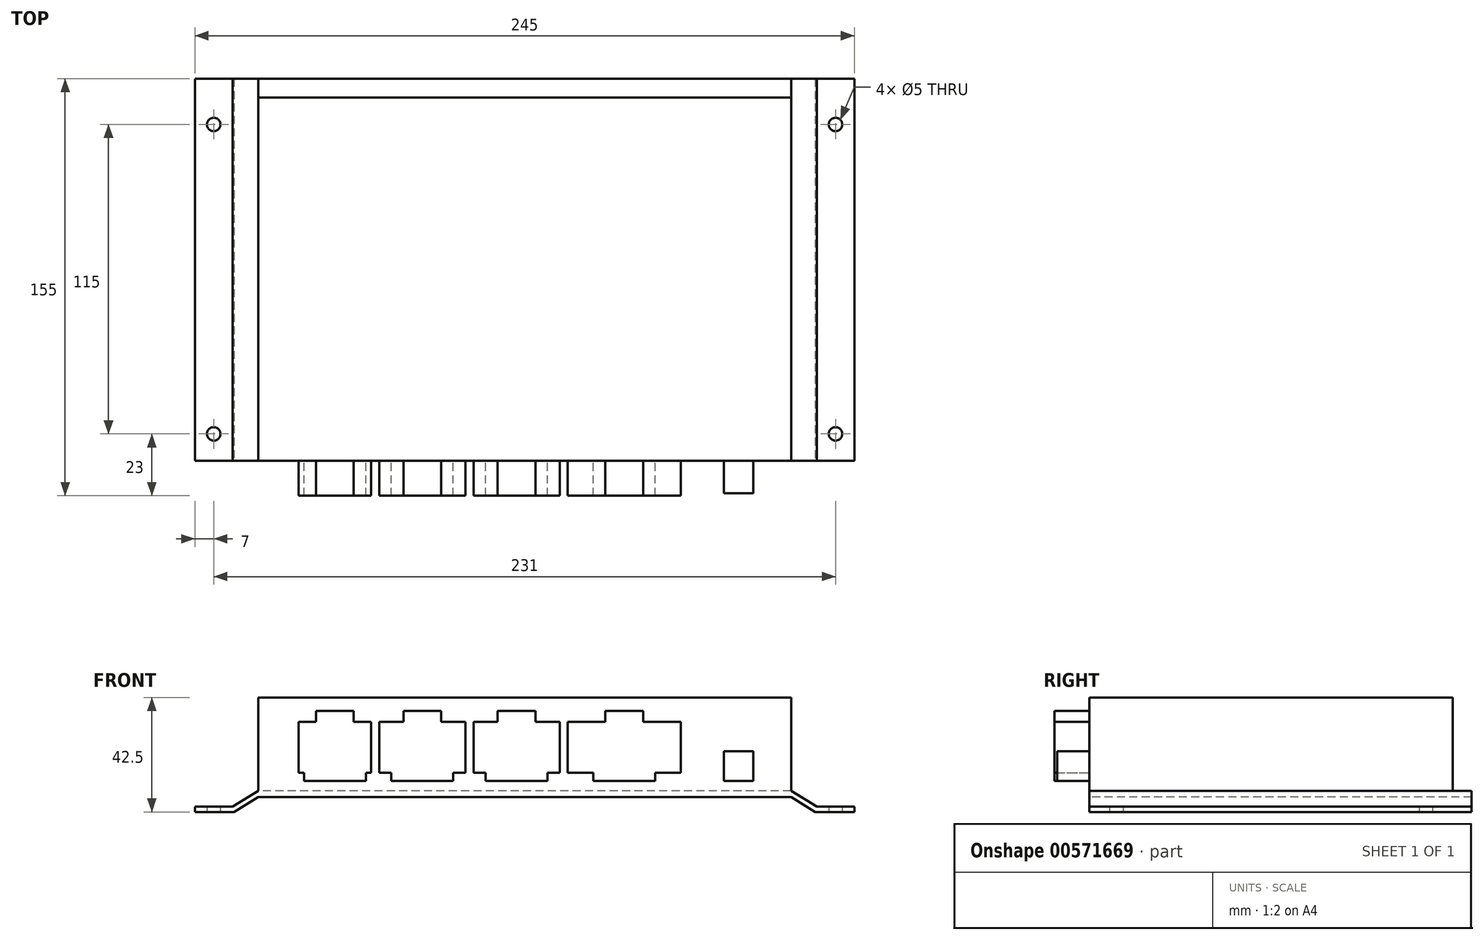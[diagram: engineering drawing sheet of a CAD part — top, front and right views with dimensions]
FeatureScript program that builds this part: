
annotation { "Feature Type Name" : "Feature", "Feature Type Description" : "" }
export const myFeature = defineFeature(function(context is Context, id is Id, definition is map)
    precondition{}
    {
        {
            var Q0;
            Q0=qCreatedBy(makeId("Top.planeOp"),FACE);
            var sketch = newSketch(context, id + "F0", { "sketchPlane" : qUnion([Q0])});
            skLineSegment(sketch, "E0.bottom", {"start": v(99, 67.5) * mm, "end": v(-99, 67.5) * mm});
            skLineSegment(sketch, "E0.top", {"start": v(99, -67.5) * mm, "end": v(-99, -67.5) * mm});
            skLineSegment(sketch, "E0.left", {"start": v(99, 67.5) * mm, "end": v(99, -67.5) * mm});
            skLineSegment(sketch, "E0.right", {"start": v(-99, 67.5) * mm, "end": v(-99, -67.5) * mm});
            skPoint(sketch, "E0.middle", {"position": v(0, 0) * mm});
            skSolve(sketch);
        }
        {
            var Q0;
            Q0=makeQuery(id+"F0.imprint","IMPRINT",FACE,{"disambiguationData":[TD([[makeQuery(id+"F0.imprint","IMPRINT",EDGE,{"derivedFrom":sQuery(id+"F0.wireOp",EDGE,"E0.bottom")}),1.0]])]});
            extrude(context, id + "F1", {"entities" : qUnion([Q0]), "depth" : 37 * mm, "offsetDistance" : 25 * mm});
        }
        {
            var Q0;
            Q0=makeQuery(id+"F1.opExtrude","SWEPT_FACE",FACE,{"disambiguationData":[OSD([sQuery(id+"F0.wireOp",EDGE,"E0.top")])]});
            var sketch = newSketch(context, id + "F2", { "sketchPlane" : qUnion([Q0])});
            skLineSegment(sketch, "E1", {"start": v(-122.5, -3.5) * mm, "end": v(-122.5, -5.5) * mm});
            skLineSegment(sketch, "E2", {"start": v(-122.5, -5.5) * mm, "end": v(-107.93, -5.5) * mm});
            skLineSegment(sketch, "E3", {"start": v(-107.93, -5.5) * mm, "end": v(-99, 0) * mm});
            skLineSegment(sketch, "E4", {"start": v(-122.5, -3.5) * mm, "end": v(-108.5, -3.5) * mm});
            skLineSegment(sketch, "E5", {"start": v(-108.5, -3.5) * mm, "end": v(-99, 2.35) * mm});
            skLineSegment(sketch, "E6", {"start": v(-99, 2.35) * mm, "end": v(-99, 0) * mm});
            skLineSegment(sketch, "E7", {"start": v(0, 37) * mm, "end": v(0, 0) * mm, "construction": true});
            skLineSegment(sketch, "E8.MirrorCS", {"start": v(99, 2.35) * mm, "end": v(99, 0) * mm});
            skLineSegment(sketch, "E9.MirrorCS", {"start": v(107.93, -5.5) * mm, "end": v(99, 0) * mm});
            skLineSegment(sketch, "E10.MirrorCS", {"start": v(108.5, -3.5) * mm, "end": v(99, 2.35) * mm});
            skLineSegment(sketch, "E11.MirrorCS", {"start": v(122.5, -3.5) * mm, "end": v(108.5, -3.5) * mm});
            skLineSegment(sketch, "E12.MirrorCS", {"start": v(122.5, -5.5) * mm, "end": v(107.93, -5.5) * mm});
            skLineSegment(sketch, "E13.MirrorCS", {"start": v(122.5, -3.5) * mm, "end": v(122.5, -5.5) * mm});
            skSolve(sketch);
        }
        {
            var Q0;
            Q0=makeQuery(id+"F2.imprint","IMPRINT",FACE,{"disambiguationData":[TD([[makeQuery(id+"F2.imprint","IMPRINT",EDGE,{"derivedFrom":sQuery(id+"F2.wireOp",EDGE,"E1")}),1.0]])]});
            var Q1;
            Q1=makeQuery(id+"F2.imprint","IMPRINT",FACE,{"disambiguationData":[TD([[makeQuery(id+"F2.imprint","IMPRINT",EDGE,{"derivedFrom":sQuery(id+"F2.wireOp",EDGE,"E8.MirrorCS")}),1.0]])]});
            var Q2;
            Q2=makeQuery(id+"F1.opExtrude","SWEPT_FACE",FACE,{"disambiguationData":[OSD([sQuery(id+"F0.wireOp",EDGE,"E0.bottom")])]});
            extrude(context, id + "F3", {"entities" : qUnion([Q0, Q1]), "operationType" : NewBodyOperationType.ADD, "endBound" : BoundingType.UP_TO_SURFACE, "oppositeDirection" : true, "depth" : 25 * mm, "endBoundEntityFace" : qUnion([Q2]), "offsetDistance" : 25 * mm});
        }
        {
            var Q0;
            Q0=makeQuery(id+"F3.opExtrude","SWEPT_FACE",FACE,{"disambiguationData":[OSD([sQuery(id+"F2.wireOp",EDGE,"E2")])]});
            var sketch = newSketch(context, id + "F4", { "sketchPlane" : qUnion([Q0])});
            skLineSegment(sketch, "E14.bottom", {"start": v(115.5, 57.5) * mm, "end": v(-115.5, 57.5) * mm, "construction": true});
            skLineSegment(sketch, "E14.top", {"start": v(115.5, -57.5) * mm, "end": v(-115.5, -57.5) * mm, "construction": true});
            skLineSegment(sketch, "E14.left", {"start": v(115.5, 57.5) * mm, "end": v(115.5, -57.5) * mm, "construction": true});
            skLineSegment(sketch, "E14.right", {"start": v(-115.5, 57.5) * mm, "end": v(-115.5, -57.5) * mm, "construction": true});
            skPoint(sketch, "E14.middle", {"position": v(0, 0) * mm});
            skCircle(sketch, "E15", {"center": v(-115.5, 57.5) * mm, "radius": 2.5 * mm});
            skCircle(sketch, "E16", {"center": v(-115.5, -57.5) * mm, "radius": 2.5 * mm});
            skCircle(sketch, "E17", {"center": v(115.5, -57.5) * mm, "radius": 2.5 * mm});
            skCircle(sketch, "E18", {"center": v(115.5, 57.5) * mm, "radius": 2.5 * mm});
            skSolve(sketch);
        }
        {
            var Q0;
            Q0=makeQuery(id+"F4.imprint","IMPRINT",FACE,{"disambiguationData":[TD([[makeQuery(id+"F4.imprint","IMPRINT",EDGE,{"derivedFrom":sQuery(id+"F4.wireOp",EDGE,"E15")}),1.0]])]});
            var Q1;
            Q1=makeQuery(id+"F4.imprint","IMPRINT",FACE,{"disambiguationData":[TD([[makeQuery(id+"F4.imprint","IMPRINT",EDGE,{"derivedFrom":sQuery(id+"F4.wireOp",EDGE,"E16")}),1.0]])]});
            var Q2;
            Q2=makeQuery(id+"F4.imprint","IMPRINT",FACE,{"disambiguationData":[TD([[makeQuery(id+"F4.imprint","IMPRINT",EDGE,{"derivedFrom":sQuery(id+"F4.wireOp",EDGE,"E17")}),1.0]])]});
            var Q3;
            Q3=makeQuery(id+"F4.imprint","IMPRINT",FACE,{"disambiguationData":[TD([[makeQuery(id+"F4.imprint","IMPRINT",EDGE,{"derivedFrom":sQuery(id+"F4.wireOp",EDGE,"E18")}),1.0]])]});
            extrude(context, id + "F5", {"entities" : qUnion([Q0, Q1, Q2, Q3]), "operationType" : NewBodyOperationType.REMOVE, "oppositeDirection" : true, "depth" : 25 * mm, "offsetDistance" : 25 * mm});
        }
        {
            var Q0;
            {var subQ0=sQuery(id+"F0.wireOp",EDGE,"E0.bottom");Q0=makeQuery(id+"F3.boolean.opBoolean","MERGE",FACE,{"derivedFrom":[makeQuery(id+"F1.opExtrude","SWEPT_FACE",FACE,{"disambiguationData":[OSD([subQ0])]}),makeQuery(id+"F3.opExtrude","CAP_FACE",FACE,{"disambiguationData":[OSD([subQ0]),OD(0.0)],"isStart":false}),makeQuery(id+"F3.opExtrude","CAP_FACE",FACE,{"disambiguationData":[OSD([subQ0]),OD(1.0)],"isStart":false})]});}
            var sketch = newSketch(context, id + "F6", { "sketchPlane" : qUnion([Q0])});
            skLineSegment(sketch, "E19", {"start": v(-107.93, -5.5) * mm, "end": v(-122.5, -5.5) * mm});
            skLineSegment(sketch, "E20", {"start": v(-122.5, -5.5) * mm, "end": v(-122.5, -3.5) * mm});
            skLineSegment(sketch, "E21", {"start": v(-122.5, -3.5) * mm, "end": v(-108.5, -3.5) * mm});
            skLineSegment(sketch, "E22", {"start": v(-108.5, -3.5) * mm, "end": v(-99, 2.35) * mm});
            skLineSegment(sketch, "E23", {"start": v(-99, 2.35) * mm, "end": v(99, 2.35) * mm});
            skLineSegment(sketch, "E24", {"start": v(99, 2.35) * mm, "end": v(108.5, -3.5) * mm});
            skLineSegment(sketch, "E25", {"start": v(108.5, -3.5) * mm, "end": v(122.5, -3.5) * mm});
            skLineSegment(sketch, "E26", {"start": v(122.5, -3.5) * mm, "end": v(122.5, -5.5) * mm});
            skLineSegment(sketch, "E27", {"start": v(122.5, -5.5) * mm, "end": v(107.93, -5.5) * mm});
            skLineSegment(sketch, "E28", {"start": v(107.93, -5.5) * mm, "end": v(99, 0) * mm});
            skLineSegment(sketch, "E29", {"start": v(99, 0) * mm, "end": v(-99, 0) * mm});
            skLineSegment(sketch, "E30", {"start": v(-99, 0) * mm, "end": v(-107.93, -5.5) * mm});
            skSolve(sketch);
        }
        {
            var Q0;
            Q0 = qSketchRegion(id + "F6", true);
            extrude(context, id + "F7", {"entities" : qUnion([Q0]), "operationType" : NewBodyOperationType.ADD, "depth" : 7 * mm, "offsetDistance" : 25 * mm});
        }
        {
            var Q0;
            Q0=makeQuery(id+"F3.boolean.opBoolean","MERGE",FACE,{"derivedFrom":[makeQuery(id+"F1.opExtrude","SWEPT_FACE",FACE,{"disambiguationData":[OSD([sQuery(id+"F0.wireOp",EDGE,"E0.top")])]}),makeQuery(id+"F3.opExtrude","CAP_FACE",FACE,{"disambiguationData":[OSD([sQuery(id+"F2.wireOp",EDGE,"E1"),sQuery(id+"F2.wireOp",EDGE,"E2"),sQuery(id+"F2.wireOp",EDGE,"E3"),sQuery(id+"F2.wireOp",EDGE,"E4"),sQuery(id+"F2.wireOp",EDGE,"E5"),sQuery(id+"F2.wireOp",EDGE,"E6")])],"isStart":true}),makeQuery(id+"F3.opExtrude","CAP_FACE",FACE,{"disambiguationData":[OSD([sQuery(id+"F2.wireOp",EDGE,"E8.MirrorCS"),sQuery(id+"F2.wireOp",EDGE,"E9.MirrorCS"),sQuery(id+"F2.wireOp",EDGE,"E10.MirrorCS"),sQuery(id+"F2.wireOp",EDGE,"E11.MirrorCS"),sQuery(id+"F2.wireOp",EDGE,"E12.MirrorCS"),sQuery(id+"F2.wireOp",EDGE,"E13.MirrorCS")])],"isStart":true})]});
            var sketch = newSketch(context, id + "F8", { "sketchPlane" : qUnion([Q0])});
            skLineSegment(sketch, "E31", {"start": v(-84, 28) * mm, "end": v(-84, 9) * mm});
            skLineSegment(sketch, "E32", {"start": v(-84, 9) * mm, "end": v(-82, 9) * mm});
            skLineSegment(sketch, "E33", {"start": v(-82, 9) * mm, "end": v(-82, 6) * mm});
            skLineSegment(sketch, "E34", {"start": v(-82, 6) * mm, "end": v(-59, 6) * mm});
            skLineSegment(sketch, "E35", {"start": v(-59, 6) * mm, "end": v(-59, 9) * mm});
            skLineSegment(sketch, "E36", {"start": v(-59, 9) * mm, "end": v(-57, 9) * mm});
            skLineSegment(sketch, "E37", {"start": v(-57, 9) * mm, "end": v(-57, 28) * mm});
            skLineSegment(sketch, "E38", {"start": v(-57, 28) * mm, "end": v(-63.5, 28) * mm});
            skLineSegment(sketch, "E39", {"start": v(-63.5, 28) * mm, "end": v(-63.5, 32) * mm});
            skLineSegment(sketch, "E40", {"start": v(-63.5, 32) * mm, "end": v(-77.5, 32) * mm});
            skLineSegment(sketch, "E41", {"start": v(-77.5, 32) * mm, "end": v(-77.5, 28) * mm});
            skLineSegment(sketch, "E42", {"start": v(-77.5, 28) * mm, "end": v(-84, 28) * mm});
            skLineSegment(sketch, "E43", {"start": v(-54, 28) * mm, "end": v(-54, 9) * mm});
            skLineSegment(sketch, "E44", {"start": v(-54, 9) * mm, "end": v(-49.5, 9) * mm});
            skLineSegment(sketch, "E45", {"start": v(-49.5, 9) * mm, "end": v(-49.5, 6) * mm});
            skLineSegment(sketch, "E46", {"start": v(-49.5, 6) * mm, "end": v(-26.5, 6) * mm});
            skLineSegment(sketch, "E47", {"start": v(-26.5, 6) * mm, "end": v(-26.5, 9) * mm});
            skLineSegment(sketch, "E48", {"start": v(-26.5, 9) * mm, "end": v(-22, 9) * mm});
            skLineSegment(sketch, "E49", {"start": v(-22, 9) * mm, "end": v(-22, 28) * mm});
            skLineSegment(sketch, "E50", {"start": v(-22, 28) * mm, "end": v(-31, 28) * mm});
            skLineSegment(sketch, "E51", {"start": v(-31, 28) * mm, "end": v(-31, 32) * mm});
            skLineSegment(sketch, "E52", {"start": v(-31, 32) * mm, "end": v(-45, 32) * mm});
            skLineSegment(sketch, "E53", {"start": v(-45, 32) * mm, "end": v(-45, 28) * mm});
            skLineSegment(sketch, "E54", {"start": v(-45, 28) * mm, "end": v(-54, 28) * mm});
            skLineSegment(sketch, "E55", {"start": v(-19, 28) * mm, "end": v(-19, 9) * mm});
            skLineSegment(sketch, "E56", {"start": v(-19, 9) * mm, "end": v(-14.5, 9) * mm});
            skLineSegment(sketch, "E57", {"start": v(-14.5, 9) * mm, "end": v(-14.5, 6) * mm});
            skLineSegment(sketch, "E58", {"start": v(-14.5, 6) * mm, "end": v(8.5, 6) * mm});
            skLineSegment(sketch, "E59", {"start": v(8.5, 6) * mm, "end": v(8.5, 9) * mm});
            skLineSegment(sketch, "E60", {"start": v(8.5, 9) * mm, "end": v(13, 9) * mm});
            skLineSegment(sketch, "E61", {"start": v(13, 9) * mm, "end": v(13, 28) * mm});
            skLineSegment(sketch, "E62", {"start": v(13, 28) * mm, "end": v(4, 28) * mm});
            skLineSegment(sketch, "E63", {"start": v(4, 28) * mm, "end": v(4, 32) * mm});
            skLineSegment(sketch, "E64", {"start": v(4, 32) * mm, "end": v(-10, 32) * mm});
            skLineSegment(sketch, "E65", {"start": v(-10, 32) * mm, "end": v(-10, 28) * mm});
            skLineSegment(sketch, "E66", {"start": v(-10, 28) * mm, "end": v(-19, 28) * mm});
            skLineSegment(sketch, "E67", {"start": v(16, 28) * mm, "end": v(16, 9) * mm});
            skLineSegment(sketch, "E68", {"start": v(16, 9) * mm, "end": v(25.5, 9) * mm});
            skLineSegment(sketch, "E69", {"start": v(25.5, 9) * mm, "end": v(25.5, 6) * mm});
            skLineSegment(sketch, "E70", {"start": v(25.5, 6) * mm, "end": v(48.5, 6) * mm});
            skLineSegment(sketch, "E71", {"start": v(48.5, 6) * mm, "end": v(48.5, 9) * mm});
            skLineSegment(sketch, "E72", {"start": v(48.5, 9) * mm, "end": v(58, 9) * mm});
            skLineSegment(sketch, "E73", {"start": v(58, 9) * mm, "end": v(58, 28) * mm});
            skLineSegment(sketch, "E74", {"start": v(58, 28) * mm, "end": v(44, 28) * mm});
            skLineSegment(sketch, "E75", {"start": v(44, 28) * mm, "end": v(44, 32) * mm});
            skLineSegment(sketch, "E76", {"start": v(44, 32) * mm, "end": v(30, 32) * mm});
            skLineSegment(sketch, "E77", {"start": v(30, 32) * mm, "end": v(30, 28) * mm});
            skLineSegment(sketch, "E78", {"start": v(30, 28) * mm, "end": v(16, 28) * mm});
            skSolve(sketch);
        }
        {
            var Q0;
            Q0=makeQuery(id+"F8.imprint","IMPRINT",FACE,{"disambiguationData":[TD([[makeQuery(id+"F8.imprint","IMPRINT",EDGE,{"derivedFrom":sQuery(id+"F8.wireOp",EDGE,"E31")}),1.0]])]});
            var Q1;
            Q1=makeQuery(id+"F8.imprint","IMPRINT",FACE,{"disambiguationData":[TD([[makeQuery(id+"F8.imprint","IMPRINT",EDGE,{"derivedFrom":sQuery(id+"F8.wireOp",EDGE,"E43")}),1.0]])]});
            var Q2;
            Q2=makeQuery(id+"F8.imprint","IMPRINT",FACE,{"disambiguationData":[TD([[makeQuery(id+"F8.imprint","IMPRINT",EDGE,{"derivedFrom":sQuery(id+"F8.wireOp",EDGE,"E55")}),1.0]])]});
            var Q3;
            Q3=makeQuery(id+"F8.imprint","IMPRINT",FACE,{"disambiguationData":[TD([[makeQuery(id+"F8.imprint","IMPRINT",EDGE,{"derivedFrom":sQuery(id+"F8.wireOp",EDGE,"E67")}),1.0]])]});
            extrude(context, id + "F9", {"entities" : qUnion([Q0, Q1, Q2, Q3]), "operationType" : NewBodyOperationType.ADD, "depth" : 13 * mm, "offsetDistance" : 25 * mm});
        }
        {
            var Q0;
            Q0=makeQuery(id+"F3.boolean.opBoolean","MERGE",FACE,{"derivedFrom":[makeQuery(id+"F1.opExtrude","SWEPT_FACE",FACE,{"disambiguationData":[OSD([sQuery(id+"F0.wireOp",EDGE,"E0.top")])]}),makeQuery(id+"F3.opExtrude","CAP_FACE",FACE,{"disambiguationData":[OSD([sQuery(id+"F2.wireOp",EDGE,"E1"),sQuery(id+"F2.wireOp",EDGE,"E2"),sQuery(id+"F2.wireOp",EDGE,"E3"),sQuery(id+"F2.wireOp",EDGE,"E4"),sQuery(id+"F2.wireOp",EDGE,"E5"),sQuery(id+"F2.wireOp",EDGE,"E6")])],"isStart":true}),makeQuery(id+"F3.opExtrude","CAP_FACE",FACE,{"disambiguationData":[OSD([sQuery(id+"F2.wireOp",EDGE,"E8.MirrorCS"),sQuery(id+"F2.wireOp",EDGE,"E9.MirrorCS"),sQuery(id+"F2.wireOp",EDGE,"E10.MirrorCS"),sQuery(id+"F2.wireOp",EDGE,"E11.MirrorCS"),sQuery(id+"F2.wireOp",EDGE,"E12.MirrorCS"),sQuery(id+"F2.wireOp",EDGE,"E13.MirrorCS")])],"isStart":true})]});
            var sketch = newSketch(context, id + "F10", { "sketchPlane" : qUnion([Q0])});
            skLineSegment(sketch, "E79.bottom", {"start": v(85, 17) * mm, "end": v(74, 17) * mm});
            skLineSegment(sketch, "E79.top", {"start": v(85, 6) * mm, "end": v(74, 6) * mm});
            skLineSegment(sketch, "E79.left", {"start": v(85, 17) * mm, "end": v(85, 6) * mm});
            skLineSegment(sketch, "E79.right", {"start": v(74, 17) * mm, "end": v(74, 6) * mm});
            skPoint(sketch, "E79.middle", {"position": v(79.5, 11.5) * mm});
            skSolve(sketch);
        }
        {
            var Q0;
            Q0=makeQuery(id+"F10.imprint","IMPRINT",FACE,{"disambiguationData":[TD([[makeQuery(id+"F10.imprint","IMPRINT",EDGE,{"derivedFrom":sQuery(id+"F10.wireOp",EDGE,"E79.bottom")}),1.0]])]});
            extrude(context, id + "F11", {"entities" : qUnion([Q0]), "operationType" : NewBodyOperationType.ADD, "depth" : 12 * mm, "offsetDistance" : 25 * mm});
        }
    });
